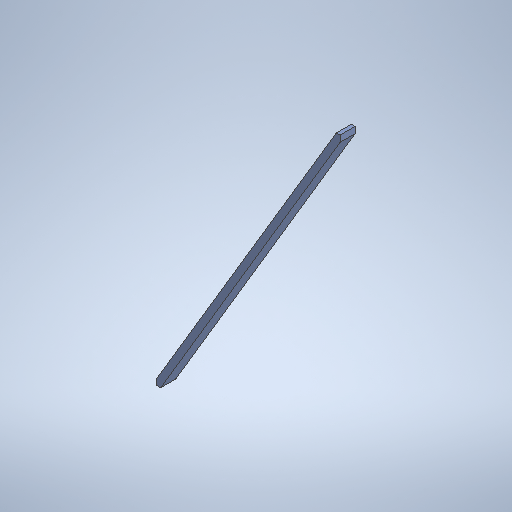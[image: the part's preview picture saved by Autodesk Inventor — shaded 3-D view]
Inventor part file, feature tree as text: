
AUTODESK INVENTOR PART (.ipt)
format: ipt  version: 2025.1 (Build 291241020, 241B)  size: 256,512 bytes
history: native  units: in
note: dims shown in document units (in); Inventor stores cm internally (conversion verified against a paired STEP export)
features: plane x1, extrude x1, sketch x1, other x1
ambient origin geometry x8: Origin, YZ Plane, XZ Plane, XY Plane, X Axis, Y Axis, Z Axis, Center Point
bodies: Solid1 (feature_tree)
feature tree (4):
  plane  "Work Plane1"
  extrude  "Extrusion1"  [1 undecoded]
  sketch  "Sketch1"  dims[d0=3.5in d1=0.0in]
  other  "Finish1"
note: 1 required parameter value undecoded (feature->parameter linkage not recoverable at this tier; creation-order binding heuristic only, values carry confidence <= 0.55)
